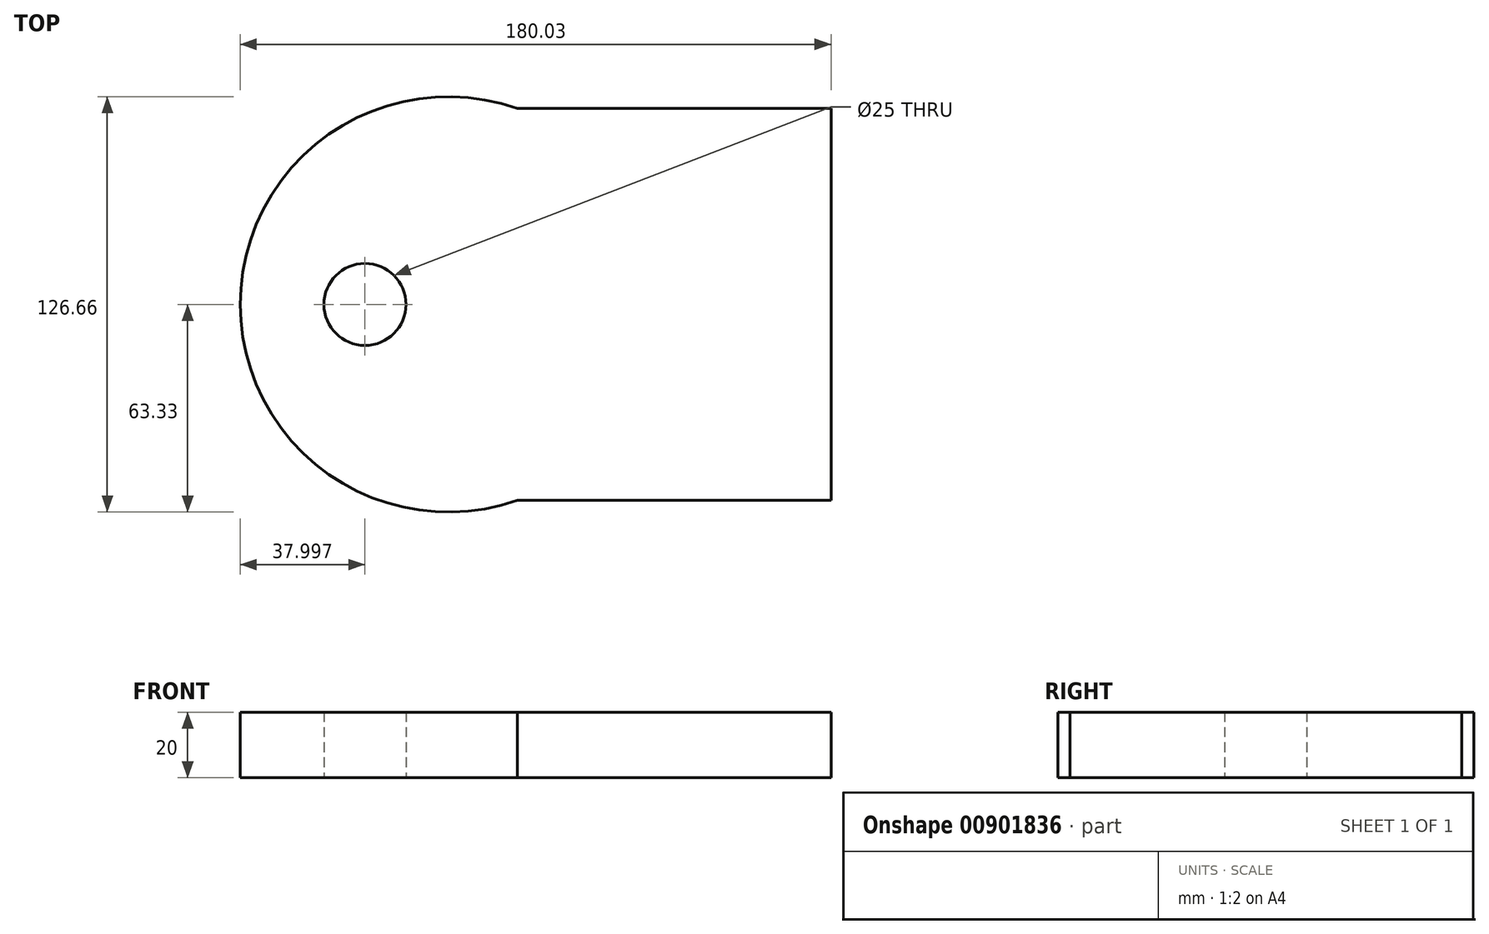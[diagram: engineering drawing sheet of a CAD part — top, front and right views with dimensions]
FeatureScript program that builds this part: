
annotation { "Feature Type Name" : "Feature", "Feature Type Description" : "" }
export const myFeature = defineFeature(function(context is Context, id is Id, definition is map)
    precondition{}
    {
        {
            var Q0;
            Q0=qCreatedBy(makeId("Top.planeOp"),FACE);
            var sketch = newSketch(context, id + "F0", { "sketchPlane" : qUnion([Q0])});
            skLineSegment(sketch, "E0", {"start": v(0, 59.71) * mm, "end": v(0, 70.5) * mm, "construction": true});
            skLineSegment(sketch, "E1", {"start": v(0, -59.71) * mm, "end": v(0, -64.92) * mm, "construction": true});
            skArc(sketch, "E2", {"start": v(-73.89, 59.71) * mm, "mid": v(-158.33, 0) * mm, "end": v(-73.89, -59.71) * mm});
            skCircle(sketch, "E3", {"center": v(-120.33, 0) * mm, "radius": 12.5 * mm});
            skLineSegment(sketch, "E4.bottom", {"start": v(-73.89, 59.71) * mm, "end": v(21.7, 59.71) * mm});
            skLineSegment(sketch, "E4.top", {"start": v(-73.89, -59.71) * mm, "end": v(21.7, -59.71) * mm});
            skLineSegment(sketch, "E4.left", {"start": v(-73.89, -59.71) * mm, "end": v(-73.89, -59.71) * mm});
            skLineSegment(sketch, "E4.right", {"start": v(21.7, 59.71) * mm, "end": v(21.7, -59.71) * mm});
            skLineSegment(sketch, "E5", {"start": v(-120.33, 0) * mm, "end": v(0, 0) * mm, "construction": true});
            skSolve(sketch);
        }
        {
            var Q0;
            Q0=makeQuery(id+"F0.imprint","IMPRINT",FACE,{"disambiguationData":[TD([[makeQuery(id+"F0.imprint","IMPRINT",EDGE,{"derivedFrom":sQuery(id+"F0.wireOp",EDGE,"t4fSHiP0-trEG-dpzW-djYr-TK3HPWNbDgth")}),-1.0]])]});
            var Q1;
            Q1=makeQuery(id+"F0.imprint","IMPRINT",FACE,{"disambiguationData":[TD([[makeQuery(id+"F0.imprint","IMPRINT",EDGE,{"derivedFrom":sQuery(id+"F0.wireOp",EDGE,"E2")}),1.0]])]});
            extrude(context, id + "F1", {"entities" : qUnion([Q0, Q1]), "depth" : 20 * mm, "offsetDistance" : 25 * mm});
        }
    });
